# Revit family: BIM_BL-9981-06
name_source: partatom
category: Aparatos sanitarios
units: mm (PartAtom-declared; Revit-internal decimal feet)

## family parameters
Activar corte en vistas = No
Anfitrión = Cara
Compartido = No
Corte con vacíos al cargar = No
Cota de conector redondo = Usar diámetro
Mantener orientación de anotación = No
Número OmniClass = 23.31.11.00
Punto de cálculo de habitación = No
Tipo de pieza = Normal

## types (1)
- 01-9983-13
    Acometida = Dim 1/2" NPT
    Alto = 46 mm
    Ancho = 75 mm
    Ancho manija llave = 48 mm  [stored 0.15748 ft]
    Conexiones = Acometida: Rosca macho ½” NPT.
Manguera: Rosca macho ¾”.
    Conexión AC = Sí
    Conexión AF = Sí
    Conexión de residuos = No
    Conexión de ventilación = No
    Consumo aproximado a 25 psi = 3.8
    Date Modified = 16-09-2025
    Descripción = Llave jardin
    Diametro Nominal = 13.9 mm
    Elevación por defecto = 0 mm  [stored 0 ft]
    Fabricante = Gricol
    Garantia Especifica = 20 años
    Imagen de tipo = LLAVE MANGUERA LIVIANA METAL SATINADA.jpg
    Link Ficha Tecnica = https://infotecnica.gricol.com
    Materiales del producto = Latón, Zamak, ABS, Polipropileno, Caucho
    Metal laton satinado = Metal Laton satinado
    Modelo = 01-9983-13
    Presión Maxima = 125.00 psi
    Presión Mínima = 20.00 psi
    Presión de Estaiildo = 500.00 psi
    Product Name = Llave Manguera Metálica Pesada Bronce
    Referente Normativo = NTC 164 4 ACCESORIOS DE SUMINISTRO EN
FONTANERÍA (ASME A112.18.1 / CSA B125.1)
    Resistencia a Corrosión = Ensayo según NTC 1156
    Salida = Dim 3/4" NH
    Sitio web = https://www.gricol.com
    Temperaturas de trabajo = 5°C a 71°C
    Tipo de Uso = Uso doméstico para agua potable.
    Torque de Conexioón = 61 Nm
    URL = https://www.gricol.com
    Vida Util = 150.000 ciclos

note: [stored X ft] marks values corroborated as IEEE doubles in the binary element streams (Revit-internal decimal feet)

## geometry (parser evidence)
native form markers: Blend x2, Sweep x8
no freeform markers — native parametric forms only
